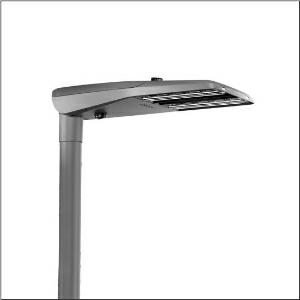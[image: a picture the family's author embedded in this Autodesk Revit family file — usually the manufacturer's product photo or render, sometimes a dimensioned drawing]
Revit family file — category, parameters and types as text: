
# Revit family: streetlight_sl_11_iq_midi___st1_2a_5xc3a21y08me_d9a7
name_source: partatom
category: Lighting Fixtures
units: mm (PartAtom-declared; Revit-internal decimal feet)

## family parameters
Cut with Voids When Loaded = No
Host = Face
Light Source = No
Part Type = Normal
Room Calculation Point = No
Round Connector Dimension = Use Diameter
Shared = No

## types (1)
- --- (1 x LED, 14840 lm, 122.8 W, 2200K)
    Apparent Load = 123 VA
    CIE Flux Codes = 32 70 96 100 100
    Color Rendering = 70
    Color Temperature = 2200K
    Default Elevation = 1800 mm
    Description = Streetlight SL 11 iQ midi, mast luminaire, primary light control with 3 zone facetted reflector, of plastic, silver coated, highly specular, primary optical cover: cover, of PMMA, transparent, light distribution: ST1.2a, light emission: direct distribution, primary light characteristic: asymmetric, installation type: post-top, side-entry, LED, High Power LED, rated luminous flux: 14.840lm, luminous efficacy: 121lm/W, light colour: 722, colour temperature: 2200K, control: presetting dimming logarithmic, Street-Remote, Auto-Match, Temp-Guard, Lumen-Switch, Night-Set, Smart-Wire, Light-Fading, Desk-Remote (wireless, voltage-free reading and setting of iQ features in the workshop via application-optimized NFC function/RFID function), optimised constant luminous flux control (CLO 2.0), with cable H07RN-F 5x 1.5mm², mains connection: 220..240V, AC, 50/60Hz, connection cable pre-assembled, cable length: 12,5m, start of lifetime: 123W, end of service life: 130W, reduction: 56W, luminaire housing, of diecast aluminium, powder-coated, Siteco® metallic grey (DB 702S), please order mast flange separately, inclination adjustable without tools: 0°, 5°, 10°, 15° (post-top) | 0°, -5°, -10°, -15° (side-entry), sealing non-destructively replaceable, multi-level sealing system, length: 780mm, width: 376mm, height: 118mm, spigot size: 60/76mm (post-top) and 42/60/76mm (side-entry), mast flange for spigot size: 42mm: 5XC10008XM4, 60mm: 5XC10008XM2, 76/60mm: 5XC10108XM1, equipment: Power, Smart Interface below and above, protection rating (complete): IP66, insulation class (complete): insulation class II (safety insulation), certification: CE, ENEC in preparation, impact resistance: IK09, permissible operating ambient temperature for outdoor applications: -25..+50°C, standard-compliant lighting for roads and squares, packaging unit: 1 piece

Light Distribution: ST1.2a
    Height = 118 mm
    Lamp = 1 x LED
    Lamp Light Flux = 14840 lm
    Lamp Power = 122.8 W
    Lamp count = 1
    Length = 780 mm
    Luminous efficacy = 121 lm/W
    Manufacturer = Siteco
    ModVariant = No
    Model = 5XC3A21Y08ME
    Number of Poles = 1
    OnlyDefault = Yes
    Power Factor = 1
    Product Name = Streetlight SL 11 iQ midi | ST1.2a
    Product group = mast luminaire | pylon top
    ProductGroupID = 6100
    Protection Class = Protection class II
    Protection Degree = IP 66
    RLX_Detail_Level = 1
    RlxData = <blob elided: 69537 chars, md5=bacccb22>
    Socket = socket
    Standby Power = 0 W
    System Light Flux = 14840 lm
    System Power = 123 W
    Type Comments = factory setting: luminous flux: 100 % | dim-lin: 254 | 553 mA
    Type Image = l_1004429.jpg
    URL = http://relux.com
    VarID = @adj_039749
    Voltage = 0 V
    Weight = 0.00 kg
    Width = 376 mm

## geometry (parser evidence)
native form markers: Blend x4, Sweep x8
no freeform markers — native parametric forms only
